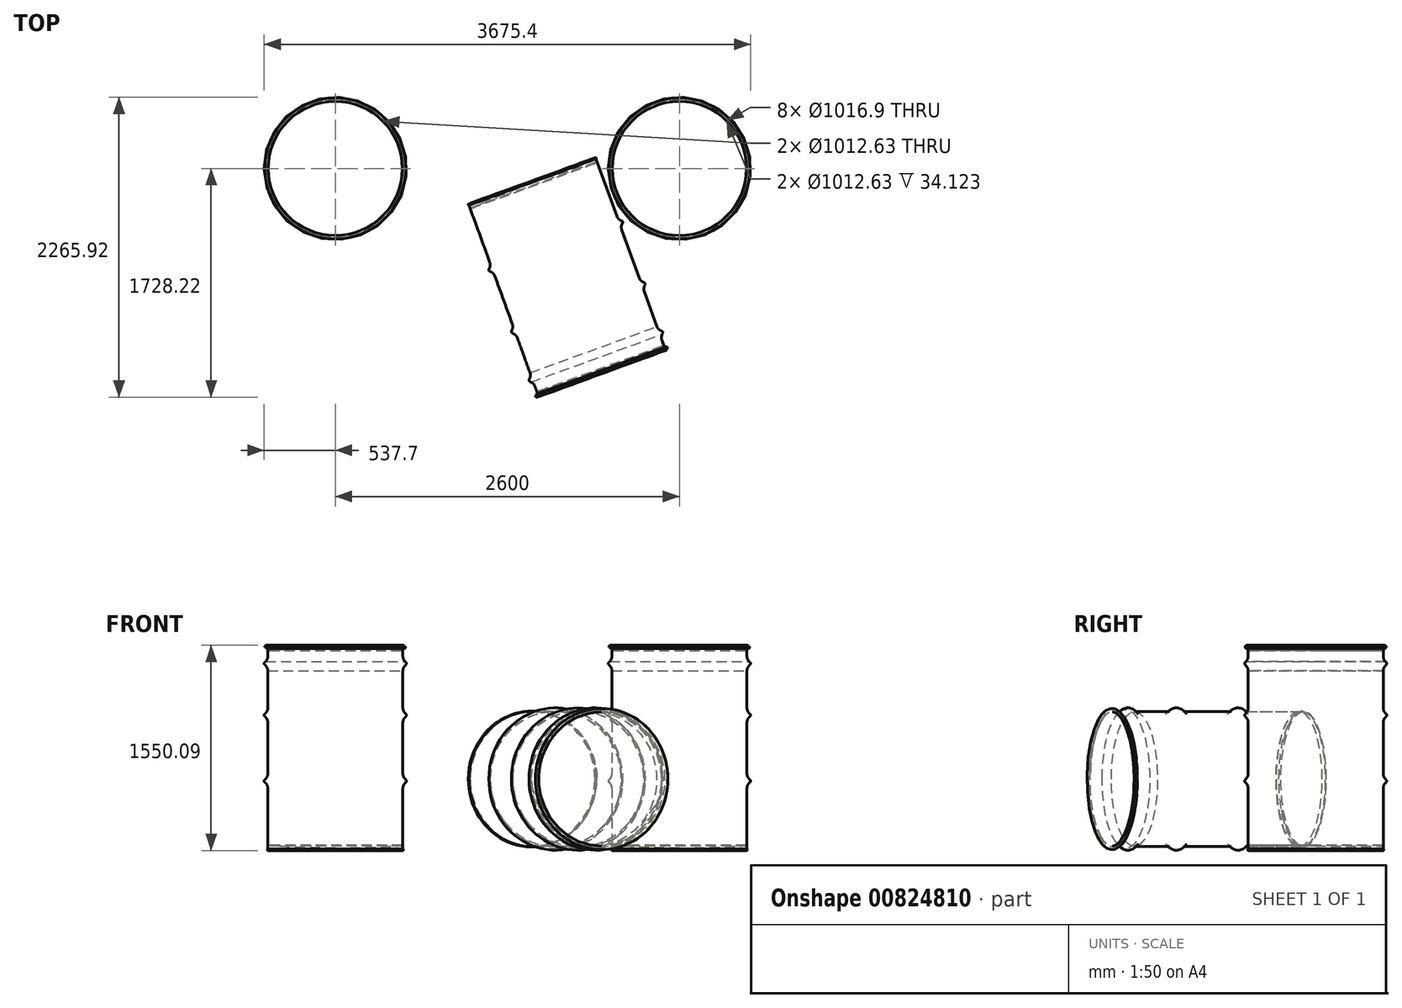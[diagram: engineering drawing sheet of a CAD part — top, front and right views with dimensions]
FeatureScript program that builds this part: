
annotation { "Feature Type Name" : "Feature", "Feature Type Description" : "" }
export const myFeature = defineFeature(function(context is Context, id is Id, definition is map)
    precondition{}
    {
        {
            var Q0;
            Q0=qCreatedBy(makeId("Front.planeOp"),FACE);
            var sketch = newSketch(context, id + "F0", { "sketchPlane" : qUnion([Q0])});
            skLineSegment(sketch, "E0.top", {"start": v(-286.95, 863.6) * mm, "end": v(-285.75, 863.6) * mm, "construction": true});
            skLineSegment(sketch, "E0.right", {"start": v(-285.75, 0) * mm, "end": v(-285.75, 264.7) * mm});
            skLineSegment(sketch, "E1", {"start": v(0, 0) * mm, "end": v(0, 177.34) * mm, "construction": true});
            skArc(sketch, "E2", {"start": v(-285.75, 863.6) * mm, "mid": v(-297.8, 866.42) * mm, "end": v(-288.25, 858.55) * mm});
            skArc(sketch, "E3", {"start": v(-286.95, 863.6) * mm, "mid": v(-296.72, 865.89) * mm, "end": v(-288.98, 859.5) * mm});
            skLineSegment(sketch, "E4", {"start": v(-288.98, 859.5) * mm, "end": v(-288.25, 858.55) * mm});
            skArc(sketch, "E5", {"start": v(-285.75, 0) * mm, "mid": v(-288.87, 2.56) * mm, "end": v(-286.95, 6.11) * mm});
            skLineSegment(sketch, "E6.trimOffspring", {"start": v(-286.95, 6.11) * mm, "end": v(-286.95, 264.7) * mm});
            skPoint(sketch, "E0.left.start.orphan", {"position": v(-286.95, 0) * mm});
            skLineSegment(sketch, "E7", {"start": v(-295.84, 802.73) * mm, "end": v(-300.33, 798.24) * mm});
            skLineSegment(sketch, "E8", {"start": v(-300.33, 789.26) * mm, "end": v(-295.84, 784.77) * mm});
            skLineSegment(sketch, "E9.trimOffspring", {"start": v(-286.95, 824.2) * mm, "end": v(-286.95, 863.6) * mm});
            skArc(sketch, "E10.filletArc", {"start": v(-300.33, 798.24) * mm, "mid": v(-302.2, 793.75) * mm, "end": v(-300.33, 789.26) * mm});
            skArc(sketch, "E11.filletArc", {"start": v(-295.84, 802.73) * mm, "mid": v(-289.26, 812.58) * mm, "end": v(-286.95, 824.2) * mm});
            skArc(sketch, "E12.filletArc", {"start": v(-286.95, 763.3) * mm, "mid": v(-289.26, 774.92) * mm, "end": v(-295.84, 784.77) * mm});
            skLineSegment(sketch, "E13", {"start": v(-302.19, 748.51) * mm, "end": v(-302.19, 170.1) * mm, "construction": true});
            skLineSegment(sketch, "E14", {"start": v(-292.1, 863.6) * mm, "end": v(-292.1, 869.95) * mm, "construction": true});
            skLineSegment(sketch, "E15", {"start": v(-300.33, 798.24) * mm, "end": v(-300.33, 789.26) * mm, "construction": true});
            skLineSegment(sketch, "E16", {"start": v(-295.84, 802.73) * mm, "end": v(-295.84, 784.77) * mm, "construction": true});
            skLineSegment(sketch, "E17", {"start": v(-286.95, 763.3) * mm, "end": v(-285.75, 763.3) * mm, "construction": true});
            skLineSegment(sketch, "E18", {"start": v(-286.95, 824.2) * mm, "end": v(-285.75, 824.2) * mm, "construction": true});
            skLineSegment(sketch, "E19.trimOffspring", {"start": v(-285.75, 824.2) * mm, "end": v(-285.75, 863.6) * mm});
            skLineSegment(sketch, "E20", {"start": v(-299.35, 790.24) * mm, "end": v(-294.86, 785.75) * mm});
            skLineSegment(sketch, "E21", {"start": v(-299.35, 797.26) * mm, "end": v(-294.86, 801.75) * mm});
            skArc(sketch, "E22", {"start": v(-299.35, 797.26) * mm, "mid": v(-300.8, 793.75) * mm, "end": v(-299.35, 790.24) * mm});
            skArc(sketch, "E23", {"start": v(-294.86, 801.75) * mm, "mid": v(-288.12, 812.08) * mm, "end": v(-285.75, 824.2) * mm});
            skArc(sketch, "E24", {"start": v(-285.75, 763.3) * mm, "mid": v(-288.03, 775.45) * mm, "end": v(-294.86, 785.75) * mm});
            skLineSegment(sketch, "E25", {"start": v(-295.84, 583.53) * mm, "end": v(-300.33, 579.04) * mm});
            skLineSegment(sketch, "E26", {"start": v(-300.33, 570.06) * mm, "end": v(-295.84, 565.57) * mm});
            skLineSegment(sketch, "E27.trimOffspring", {"start": v(-286.95, 605) * mm, "end": v(-286.95, 763.3) * mm});
            skPoint(sketch, "E28.visualSharp", {"position": v(-304.82, 574.55) * mm});
            skArc(sketch, "E28.filletArc", {"start": v(-300.33, 579.04) * mm, "mid": v(-302.2, 574.55) * mm, "end": v(-300.33, 570.06) * mm});
            skArc(sketch, "E29.filletArc", {"start": v(-295.84, 583.53) * mm, "mid": v(-289.26, 593.38) * mm, "end": v(-286.95, 605) * mm});
            skArc(sketch, "E30.filletArc", {"start": v(-286.95, 544.1) * mm, "mid": v(-289.26, 555.72) * mm, "end": v(-295.84, 565.57) * mm});
            skLineSegment(sketch, "E31", {"start": v(-295.84, 583.53) * mm, "end": v(-295.84, 565.57) * mm, "construction": true});
            skLineSegment(sketch, "E32", {"start": v(-286.95, 544.1) * mm, "end": v(-285.75, 544.1) * mm, "construction": true});
            skLineSegment(sketch, "E33", {"start": v(-286.95, 605) * mm, "end": v(-285.75, 605) * mm, "construction": true});
            skLineSegment(sketch, "E34.trimOffspring", {"start": v(-285.75, 605) * mm, "end": v(-285.75, 763.3) * mm});
            skLineSegment(sketch, "E35", {"start": v(-299.48, 578.19) * mm, "end": v(-295, 582.68) * mm});
            skArc(sketch, "E36", {"start": v(-295, 582.68) * mm, "mid": v(-288.15, 592.92) * mm, "end": v(-285.75, 605) * mm});
            skLineSegment(sketch, "E37", {"start": v(-299.48, 570.9) * mm, "end": v(-295, 566.42) * mm});
            skArc(sketch, "E38", {"start": v(-285.75, 544.1) * mm, "mid": v(-288.15, 556.18) * mm, "end": v(-295, 566.42) * mm});
            skArc(sketch, "E39", {"start": v(-299.48, 578.19) * mm, "mid": v(-301, 574.55) * mm, "end": v(-299.48, 570.9) * mm});
            skLineSegment(sketch, "E40", {"start": v(-295.84, 304.13) * mm, "end": v(-300.33, 299.64) * mm});
            skLineSegment(sketch, "E41", {"start": v(-300.33, 290.66) * mm, "end": v(-295.84, 286.17) * mm});
            skArc(sketch, "E42.filletArc", {"start": v(-300.33, 299.64) * mm, "mid": v(-302.19, 295.15) * mm, "end": v(-300.33, 290.66) * mm});
            skLineSegment(sketch, "E43.trimOffspring", {"start": v(-286.95, 325.6) * mm, "end": v(-286.95, 544.1) * mm});
            skArc(sketch, "E44.filletArc", {"start": v(-295.84, 304.13) * mm, "mid": v(-289.26, 313.98) * mm, "end": v(-286.95, 325.6) * mm});
            skArc(sketch, "E45.filletArc", {"start": v(-286.95, 264.7) * mm, "mid": v(-289.26, 276.32) * mm, "end": v(-295.84, 286.17) * mm});
            skLineSegment(sketch, "E46", {"start": v(-300.33, 299.64) * mm, "end": v(-300.33, 290.66) * mm, "construction": true});
            skLineSegment(sketch, "E47", {"start": v(-295.84, 304.13) * mm, "end": v(-295.84, 286.17) * mm, "construction": true});
            skLineSegment(sketch, "E48", {"start": v(-286.95, 325.6) * mm, "end": v(-285.75, 325.6) * mm, "construction": true});
            skLineSegment(sketch, "E49", {"start": v(-286.95, 264.7) * mm, "end": v(-285.75, 264.7) * mm, "construction": true});
            skLineSegment(sketch, "E50.trimOffspring", {"start": v(-285.75, 325.6) * mm, "end": v(-285.75, 544.1) * mm});
            skLineSegment(sketch, "E51", {"start": v(-299.48, 298.79) * mm, "end": v(-295, 303.28) * mm});
            skLineSegment(sketch, "E52", {"start": v(-299.48, 291.5) * mm, "end": v(-295, 287.02) * mm});
            skArc(sketch, "E53", {"start": v(-295, 303.28) * mm, "mid": v(-288.15, 313.52) * mm, "end": v(-285.75, 325.6) * mm});
            skArc(sketch, "E54", {"start": v(-285.75, 264.7) * mm, "mid": v(-288.15, 276.78) * mm, "end": v(-295, 287.02) * mm});
            skArc(sketch, "E55", {"start": v(-299.48, 298.79) * mm, "mid": v(-300.99, 295.15) * mm, "end": v(-299.48, 291.5) * mm});
            skLineSegment(sketch, "E56", {"start": v(0, 0) * mm, "end": v(-491.48, 0) * mm, "construction": true});
            skSolve(sketch);
        }
        {
            var Q0;
            Q0=qSketchRegion(id+"F0",true);
            var Q1;
            Q1=qConstructionFilter(qBodyType(qCreatedBy(id+"F0",EDGE),BodyType.WIRE),ConstructionObject.NO);
            var Q2;
            Q2=sQuery(id+"F0.wireOp",EDGE,"E1");
            revolve(context, id + "F1", {"entities" : qUnion([Q0]), "surfaceEntities" : qUnion([Q1]), "axis" : qUnion([Q2]), "revolveType" : RevolveType.FULL});
        }
        {
            var Q0;
            Q0=qCreatedBy(makeId("Front.planeOp"),FACE);
            var sketch = newSketch(context, id + "F2", { "sketchPlane" : qUnion([Q0])});
            skLineSegment(sketch, "E57", {"start": v(286.95, 6.11) * mm, "end": v(286.95, 264.7) * mm});
            skArc(sketch, "E58", {"start": v(285.75, 0) * mm, "mid": v(288.87, 2.56) * mm, "end": v(286.95, 6.11) * mm});
            skLineSegment(sketch, "E59", {"start": v(285.75, 0) * mm, "end": v(285.75, 264.7) * mm});
            skLineSegment(sketch, "E60", {"start": v(-285.75, 264.7) * mm, "end": v(-285.75, 0) * mm});
            skLineSegment(sketch, "E61", {"start": v(-285.75, 0) * mm, "end": v(-284.55, 0) * mm});
            skLineSegment(sketch, "E62", {"start": v(-284.55, 0) * mm, "end": v(-284.55, 19.18) * mm});
            skArc(sketch, "E63", {"start": v(-282.4, 21.14) * mm, "mid": v(-283.91, 20.63) * mm, "end": v(-284.55, 19.18) * mm});
            skLineSegment(sketch, "E64", {"start": v(0, 244.83) * mm, "end": v(0, -50.53) * mm, "construction": true});
            skArc(sketch, "E65", {"start": v(-282.4, 21.14) * mm, "mid": v(-141.33, 12.15) * mm, "end": v(0, 9.14) * mm});
            skLineSegment(sketch, "E66", {"start": v(0, 9.14) * mm, "end": v(0, 10.34) * mm});
            skArc(sketch, "E67", {"start": v(-285.75, 19.18) * mm, "mid": v(-284.72, 21.52) * mm, "end": v(-282.3, 22.34) * mm});
            skArc(sketch, "E68", {"start": v(-282.3, 22.34) * mm, "mid": v(-141.28, 13.34) * mm, "end": v(0, 10.34) * mm});
            skLineSegment(sketch, "E69", {"start": v(-282.58, 19.18) * mm, "end": v(-282.58, 22.35) * mm, "construction": true});
            skSolve(sketch);
        }
        {
            var Q0;
            Q0=qSketchRegion(id+"F2",true);
            var Q1;
            Q1=sQuery(id+"F2.wireOp",EDGE,"E64");
            revolve(context, id + "F3", {"operationType" : NewBodyOperationType.ADD, "entities" : qUnion([Q0]), "axis" : qUnion([Q1]), "revolveType" : RevolveType.FULL});
        }
        {
            var Q0;
            Q0=qCreatedBy(makeId("Front.planeOp"),FACE);
            var sketch = newSketch(context, id + "F4", { "sketchPlane" : qUnion([Q0])});
            skLineSegment(sketch, "E70", {"start": v(0, 998.16) * mm, "end": v(0, -198.69) * mm, "construction": true});
            skArc(sketch, "E71", {"start": v(-288.25, 858.55) * mm, "mid": v(-297.8, 866.42) * mm, "end": v(-285.75, 863.6) * mm, "construction": true});
            skLineSegment(sketch, "E72", {"start": v(-285.75, 863.6) * mm, "end": v(-285.75, 824.2) * mm, "construction": true});
            skArc(sketch, "E73", {"start": v(-298.45, 863.6) * mm, "mid": v(-292.1, 869.95) * mm, "end": v(-285.75, 863.6) * mm});
            skLineSegment(sketch, "E74", {"start": v(-285.75, 863.6) * mm, "end": v(-285.75, 855.15) * mm});
            skArc(sketch, "E75", {"start": v(-285.75, 855.15) * mm, "mid": v(-283.75, 850.52) * mm, "end": v(-279.02, 848.8) * mm});
            skArc(sketch, "E76", {"start": v(-279.02, 848.8) * mm, "mid": v(-139.57, 855.14) * mm, "end": v(0, 857.25) * mm});
            skLineSegment(sketch, "E77", {"start": v(-298.45, 863.6) * mm, "end": v(-299.65, 863.6) * mm});
            skArc(sketch, "E78", {"start": v(-299.65, 863.6) * mm, "mid": v(-292.1, 871.15) * mm, "end": v(-284.55, 863.6) * mm});
            skLineSegment(sketch, "E79", {"start": v(-284.55, 863.6) * mm, "end": v(-284.55, 855.15) * mm});
            skArc(sketch, "E80", {"start": v(-284.55, 855.15) * mm, "mid": v(-282.93, 851.4) * mm, "end": v(-279.09, 850) * mm});
            skArc(sketch, "E81", {"start": v(-279.09, 850) * mm, "mid": v(-139.6, 856.34) * mm, "end": v(0, 858.45) * mm});
            skLineSegment(sketch, "E82", {"start": v(0, 858.45) * mm, "end": v(0, 857.25) * mm});
            skLineSegment(sketch, "E83", {"start": v(-279.4, 855.15) * mm, "end": v(-279.02, 848.8) * mm, "construction": true});
            skLineSegment(sketch, "E84", {"start": v(-279.4, 855.15) * mm, "end": v(-279.4, 848.8) * mm, "construction": true});
            skLineSegment(sketch, "E85", {"start": v(-292.1, 863.6) * mm, "end": v(-292.1, 871.15) * mm, "construction": true});
            skSolve(sketch);
        }
        {
            var Q0;
            Q0=qSketchRegion(id+"F4",true);
            var Q1;
            Q1=sQuery(id+"F4.wireOp",EDGE,"E70");
            revolve(context, id + "F5", {"entities" : qUnion([Q0]), "axis" : qUnion([Q1]), "revolveType" : RevolveType.FULL});
        }
        {
            var Q0;
            Q0=makeQuery(id+"F5.opRevolve","SWEPT_BODY",BODY,{"disambiguationData":[OSD([sQuery(id+"F4.wireOp",EDGE,"E73"),sQuery(id+"F4.wireOp",EDGE,"E74"),sQuery(id+"F4.wireOp",EDGE,"E75"),sQuery(id+"F4.wireOp",EDGE,"E76"),sQuery(id+"F4.wireOp",EDGE,"E77"),sQuery(id+"F4.wireOp",EDGE,"E78"),sQuery(id+"F4.wireOp",EDGE,"E79"),sQuery(id+"F4.wireOp",EDGE,"E80"),sQuery(id+"F4.wireOp",EDGE,"E81"),sQuery(id+"F4.wireOp",EDGE,"E82")])]});
            var Q1;
            Q1=makeQuery(id+"F1.opRevolve","SWEPT_BODY",BODY,{"disambiguationData":[OSD([sQuery(id+"F0.wireOp",EDGE,"E0.right"),sQuery(id+"F0.wireOp",EDGE,"E2"),sQuery(id+"F0.wireOp",EDGE,"E3"),sQuery(id+"F0.wireOp",EDGE,"E4"),sQuery(id+"F0.wireOp",EDGE,"E5"),sQuery(id+"F0.wireOp",EDGE,"E6.trimOffspring"),sQuery(id+"F0.wireOp",EDGE,"E7"),sQuery(id+"F0.wireOp",EDGE,"E8"),sQuery(id+"F0.wireOp",EDGE,"E9.trimOffspring"),sQuery(id+"F0.wireOp",EDGE,"E10.filletArc"),sQuery(id+"F0.wireOp",EDGE,"E11.filletArc"),sQuery(id+"F0.wireOp",EDGE,"E12.filletArc"),sQuery(id+"F0.wireOp",EDGE,"E19.trimOffspring"),sQuery(id+"F0.wireOp",EDGE,"E20"),sQuery(id+"F0.wireOp",EDGE,"E21"),sQuery(id+"F0.wireOp",EDGE,"E22"),sQuery(id+"F0.wireOp",EDGE,"E23"),sQuery(id+"F0.wireOp",EDGE,"E24"),sQuery(id+"F0.wireOp",EDGE,"E25"),sQuery(id+"F0.wireOp",EDGE,"E26"),sQuery(id+"F0.wireOp",EDGE,"E27.trimOffspring"),sQuery(id+"F0.wireOp",EDGE,"E28.filletArc"),sQuery(id+"F0.wireOp",EDGE,"E29.filletArc"),sQuery(id+"F0.wireOp",EDGE,"E30.filletArc"),sQuery(id+"F0.wireOp",EDGE,"E34.trimOffspring"),sQuery(id+"F0.wireOp",EDGE,"E35"),sQuery(id+"F0.wireOp",EDGE,"E36"),sQuery(id+"F0.wireOp",EDGE,"E37"),sQuery(id+"F0.wireOp",EDGE,"E38"),sQuery(id+"F0.wireOp",EDGE,"E39"),sQuery(id+"F0.wireOp",EDGE,"E40"),sQuery(id+"F0.wireOp",EDGE,"E41"),sQuery(id+"F0.wireOp",EDGE,"E42.filletArc"),sQuery(id+"F0.wireOp",EDGE,"E43.trimOffspring"),sQuery(id+"F0.wireOp",EDGE,"E44.filletArc"),sQuery(id+"F0.wireOp",EDGE,"E45.filletArc"),sQuery(id+"F0.wireOp",EDGE,"E50.trimOffspring"),sQuery(id+"F0.wireOp",EDGE,"E51"),sQuery(id+"F0.wireOp",EDGE,"E52"),sQuery(id+"F0.wireOp",EDGE,"E53"),sQuery(id+"F0.wireOp",EDGE,"E54"),sQuery(id+"F0.wireOp",EDGE,"E55")])]});
            var Q2;
            Q2=qCreatedBy(makeId("Origin.pointOp"),VERTEX);
            transform(context, id + "F6", {"entities" : qUnion([Q0, Q1]), "transformType" : TransformType.SCALE_UNIFORMLY, "scale" : 1.78, "scalePoint" : qUnion([Q2]), "makeCopy" : false});
        }
        {
            var Q0;
            Q0=makeQuery(id+"F1.opRevolve","SWEPT_BODY",BODY,{"disambiguationData":[OSD([sQuery(id+"F0.wireOp",EDGE,"E0.right"),sQuery(id+"F0.wireOp",EDGE,"E2"),sQuery(id+"F0.wireOp",EDGE,"E3"),sQuery(id+"F0.wireOp",EDGE,"E4"),sQuery(id+"F0.wireOp",EDGE,"E5"),sQuery(id+"F0.wireOp",EDGE,"E6.trimOffspring"),sQuery(id+"F0.wireOp",EDGE,"E7"),sQuery(id+"F0.wireOp",EDGE,"E8"),sQuery(id+"F0.wireOp",EDGE,"E9.trimOffspring"),sQuery(id+"F0.wireOp",EDGE,"E10.filletArc"),sQuery(id+"F0.wireOp",EDGE,"E11.filletArc"),sQuery(id+"F0.wireOp",EDGE,"E12.filletArc"),sQuery(id+"F0.wireOp",EDGE,"E19.trimOffspring"),sQuery(id+"F0.wireOp",EDGE,"E20"),sQuery(id+"F0.wireOp",EDGE,"E21"),sQuery(id+"F0.wireOp",EDGE,"E22"),sQuery(id+"F0.wireOp",EDGE,"E23"),sQuery(id+"F0.wireOp",EDGE,"E24"),sQuery(id+"F0.wireOp",EDGE,"E25"),sQuery(id+"F0.wireOp",EDGE,"E26"),sQuery(id+"F0.wireOp",EDGE,"E27.trimOffspring"),sQuery(id+"F0.wireOp",EDGE,"E28.filletArc"),sQuery(id+"F0.wireOp",EDGE,"E29.filletArc"),sQuery(id+"F0.wireOp",EDGE,"E30.filletArc"),sQuery(id+"F0.wireOp",EDGE,"E34.trimOffspring"),sQuery(id+"F0.wireOp",EDGE,"E35"),sQuery(id+"F0.wireOp",EDGE,"E36"),sQuery(id+"F0.wireOp",EDGE,"E37"),sQuery(id+"F0.wireOp",EDGE,"E38"),sQuery(id+"F0.wireOp",EDGE,"E39"),sQuery(id+"F0.wireOp",EDGE,"E40"),sQuery(id+"F0.wireOp",EDGE,"E41"),sQuery(id+"F0.wireOp",EDGE,"E42.filletArc"),sQuery(id+"F0.wireOp",EDGE,"E43.trimOffspring"),sQuery(id+"F0.wireOp",EDGE,"E44.filletArc"),sQuery(id+"F0.wireOp",EDGE,"E45.filletArc"),sQuery(id+"F0.wireOp",EDGE,"E50.trimOffspring"),sQuery(id+"F0.wireOp",EDGE,"E51"),sQuery(id+"F0.wireOp",EDGE,"E52"),sQuery(id+"F0.wireOp",EDGE,"E53"),sQuery(id+"F0.wireOp",EDGE,"E54"),sQuery(id+"F0.wireOp",EDGE,"E55")])]});
            var Q1;
            Q1=makeQuery(id+"F5.opRevolve","SWEPT_BODY",BODY,{"disambiguationData":[OSD([sQuery(id+"F4.wireOp",EDGE,"E73"),sQuery(id+"F4.wireOp",EDGE,"E74"),sQuery(id+"F4.wireOp",EDGE,"E75"),sQuery(id+"F4.wireOp",EDGE,"E76"),sQuery(id+"F4.wireOp",EDGE,"E77"),sQuery(id+"F4.wireOp",EDGE,"E78"),sQuery(id+"F4.wireOp",EDGE,"E79"),sQuery(id+"F4.wireOp",EDGE,"E80"),sQuery(id+"F4.wireOp",EDGE,"E81"),sQuery(id+"F4.wireOp",EDGE,"E82")])]});
            transform(context, id + "F7", {"entities" : qUnion([Q0, Q1]), "transformType" : TransformType.TRANSLATION_3D, "dx" : 2600 * mm, "dy" : 0 * mm, "dz" : 0 * mm, "makeCopy" : true});
        }
        {
            var Q0;
            Q0=makeQuery(id+"F7.opPattern","COPY",BODY,{"derivedFrom":makeQuery(id+"F5.opRevolve","SWEPT_BODY",BODY,{"disambiguationData":[OSD([sQuery(id+"F4.wireOp",EDGE,"E73"),sQuery(id+"F4.wireOp",EDGE,"E74"),sQuery(id+"F4.wireOp",EDGE,"E75"),sQuery(id+"F4.wireOp",EDGE,"E76"),sQuery(id+"F4.wireOp",EDGE,"E77"),sQuery(id+"F4.wireOp",EDGE,"E78"),sQuery(id+"F4.wireOp",EDGE,"E79"),sQuery(id+"F4.wireOp",EDGE,"E80"),sQuery(id+"F4.wireOp",EDGE,"E81"),sQuery(id+"F4.wireOp",EDGE,"E82")])]}),"instanceName":"1"});
            var Q1;
            Q1=makeQuery(id+"F7.opPattern","COPY",BODY,{"derivedFrom":makeQuery(id+"F1.opRevolve","SWEPT_BODY",BODY,{"disambiguationData":[OSD([sQuery(id+"F0.wireOp",EDGE,"E0.right"),sQuery(id+"F0.wireOp",EDGE,"E2"),sQuery(id+"F0.wireOp",EDGE,"E3"),sQuery(id+"F0.wireOp",EDGE,"E4"),sQuery(id+"F0.wireOp",EDGE,"E5"),sQuery(id+"F0.wireOp",EDGE,"E6.trimOffspring"),sQuery(id+"F0.wireOp",EDGE,"E7"),sQuery(id+"F0.wireOp",EDGE,"E8"),sQuery(id+"F0.wireOp",EDGE,"E9.trimOffspring"),sQuery(id+"F0.wireOp",EDGE,"E10.filletArc"),sQuery(id+"F0.wireOp",EDGE,"E11.filletArc"),sQuery(id+"F0.wireOp",EDGE,"E12.filletArc"),sQuery(id+"F0.wireOp",EDGE,"E19.trimOffspring"),sQuery(id+"F0.wireOp",EDGE,"E20"),sQuery(id+"F0.wireOp",EDGE,"E21"),sQuery(id+"F0.wireOp",EDGE,"E22"),sQuery(id+"F0.wireOp",EDGE,"E23"),sQuery(id+"F0.wireOp",EDGE,"E24"),sQuery(id+"F0.wireOp",EDGE,"E25"),sQuery(id+"F0.wireOp",EDGE,"E26"),sQuery(id+"F0.wireOp",EDGE,"E27.trimOffspring"),sQuery(id+"F0.wireOp",EDGE,"E28.filletArc"),sQuery(id+"F0.wireOp",EDGE,"E29.filletArc"),sQuery(id+"F0.wireOp",EDGE,"E30.filletArc"),sQuery(id+"F0.wireOp",EDGE,"E34.trimOffspring"),sQuery(id+"F0.wireOp",EDGE,"E35"),sQuery(id+"F0.wireOp",EDGE,"E36"),sQuery(id+"F0.wireOp",EDGE,"E37"),sQuery(id+"F0.wireOp",EDGE,"E38"),sQuery(id+"F0.wireOp",EDGE,"E39"),sQuery(id+"F0.wireOp",EDGE,"E40"),sQuery(id+"F0.wireOp",EDGE,"E41"),sQuery(id+"F0.wireOp",EDGE,"E42.filletArc"),sQuery(id+"F0.wireOp",EDGE,"E43.trimOffspring"),sQuery(id+"F0.wireOp",EDGE,"E44.filletArc"),sQuery(id+"F0.wireOp",EDGE,"E45.filletArc"),sQuery(id+"F0.wireOp",EDGE,"E50.trimOffspring"),sQuery(id+"F0.wireOp",EDGE,"E51"),sQuery(id+"F0.wireOp",EDGE,"E52"),sQuery(id+"F0.wireOp",EDGE,"E53"),sQuery(id+"F0.wireOp",EDGE,"E54"),sQuery(id+"F0.wireOp",EDGE,"E55")])]}),"instanceName":"1"});
            transform(context, id + "F8", {"entities" : qUnion([Q0, Q1]), "transformType" : TransformType.TRANSLATION_3D, "dx" : -1000 * mm, "dy" : -500 * mm, "dz" : 0 * mm, "makeCopy" : true});
        }
        {
            var Q0;
            Q0=makeQuery(id+"F8.opPattern","COPY",BODY,{"derivedFrom":makeQuery(id+"F7.opPattern","COPY",BODY,{"derivedFrom":makeQuery(id+"F5.opRevolve","SWEPT_BODY",BODY,{"disambiguationData":[OSD([sQuery(id+"F4.wireOp",EDGE,"E73"),sQuery(id+"F4.wireOp",EDGE,"E74"),sQuery(id+"F4.wireOp",EDGE,"E75"),sQuery(id+"F4.wireOp",EDGE,"E76"),sQuery(id+"F4.wireOp",EDGE,"E77"),sQuery(id+"F4.wireOp",EDGE,"E78"),sQuery(id+"F4.wireOp",EDGE,"E79"),sQuery(id+"F4.wireOp",EDGE,"E80"),sQuery(id+"F4.wireOp",EDGE,"E81"),sQuery(id+"F4.wireOp",EDGE,"E82")])]}),"instanceName":"1"}),"instanceName":"1"});
            var Q1;
            Q1=makeQuery(id+"F8.opPattern","COPY",BODY,{"derivedFrom":makeQuery(id+"F7.opPattern","COPY",BODY,{"derivedFrom":makeQuery(id+"F1.opRevolve","SWEPT_BODY",BODY,{"disambiguationData":[OSD([sQuery(id+"F0.wireOp",EDGE,"E0.right"),sQuery(id+"F0.wireOp",EDGE,"E2"),sQuery(id+"F0.wireOp",EDGE,"E3"),sQuery(id+"F0.wireOp",EDGE,"E4"),sQuery(id+"F0.wireOp",EDGE,"E5"),sQuery(id+"F0.wireOp",EDGE,"E6.trimOffspring"),sQuery(id+"F0.wireOp",EDGE,"E7"),sQuery(id+"F0.wireOp",EDGE,"E8"),sQuery(id+"F0.wireOp",EDGE,"E9.trimOffspring"),sQuery(id+"F0.wireOp",EDGE,"E10.filletArc"),sQuery(id+"F0.wireOp",EDGE,"E11.filletArc"),sQuery(id+"F0.wireOp",EDGE,"E12.filletArc"),sQuery(id+"F0.wireOp",EDGE,"E19.trimOffspring"),sQuery(id+"F0.wireOp",EDGE,"E20"),sQuery(id+"F0.wireOp",EDGE,"E21"),sQuery(id+"F0.wireOp",EDGE,"E22"),sQuery(id+"F0.wireOp",EDGE,"E23"),sQuery(id+"F0.wireOp",EDGE,"E24"),sQuery(id+"F0.wireOp",EDGE,"E25"),sQuery(id+"F0.wireOp",EDGE,"E26"),sQuery(id+"F0.wireOp",EDGE,"E27.trimOffspring"),sQuery(id+"F0.wireOp",EDGE,"E28.filletArc"),sQuery(id+"F0.wireOp",EDGE,"E29.filletArc"),sQuery(id+"F0.wireOp",EDGE,"E30.filletArc"),sQuery(id+"F0.wireOp",EDGE,"E34.trimOffspring"),sQuery(id+"F0.wireOp",EDGE,"E35"),sQuery(id+"F0.wireOp",EDGE,"E36"),sQuery(id+"F0.wireOp",EDGE,"E37"),sQuery(id+"F0.wireOp",EDGE,"E38"),sQuery(id+"F0.wireOp",EDGE,"E39"),sQuery(id+"F0.wireOp",EDGE,"E40"),sQuery(id+"F0.wireOp",EDGE,"E41"),sQuery(id+"F0.wireOp",EDGE,"E42.filletArc"),sQuery(id+"F0.wireOp",EDGE,"E43.trimOffspring"),sQuery(id+"F0.wireOp",EDGE,"E44.filletArc"),sQuery(id+"F0.wireOp",EDGE,"E45.filletArc"),sQuery(id+"F0.wireOp",EDGE,"E50.trimOffspring"),sQuery(id+"F0.wireOp",EDGE,"E51"),sQuery(id+"F0.wireOp",EDGE,"E52"),sQuery(id+"F0.wireOp",EDGE,"E53"),sQuery(id+"F0.wireOp",EDGE,"E54"),sQuery(id+"F0.wireOp",EDGE,"E55")])]}),"instanceName":"1"}),"instanceName":"1"});
            var Q2;
            Q2=sQuery(id+"F0.wireOp",EDGE,"E56");
            transform(context, id + "F9", {"entities" : qUnion([Q0, Q1]), "transformType" : TransformType.ROTATION, "transformAxis" : qUnion([Q2]), "angle" : 90 * degree, "oppositeDirection" : true, "makeCopy" : false});
        }
        {
            var Q0;
            Q0=makeQuery(id+"F8.opPattern","COPY",BODY,{"derivedFrom":makeQuery(id+"F7.opPattern","COPY",BODY,{"derivedFrom":makeQuery(id+"F1.opRevolve","SWEPT_BODY",BODY,{"disambiguationData":[OSD([sQuery(id+"F0.wireOp",EDGE,"E0.right"),sQuery(id+"F0.wireOp",EDGE,"E2"),sQuery(id+"F0.wireOp",EDGE,"E3"),sQuery(id+"F0.wireOp",EDGE,"E4"),sQuery(id+"F0.wireOp",EDGE,"E5"),sQuery(id+"F0.wireOp",EDGE,"E6.trimOffspring"),sQuery(id+"F0.wireOp",EDGE,"E7"),sQuery(id+"F0.wireOp",EDGE,"E8"),sQuery(id+"F0.wireOp",EDGE,"E9.trimOffspring"),sQuery(id+"F0.wireOp",EDGE,"E10.filletArc"),sQuery(id+"F0.wireOp",EDGE,"E11.filletArc"),sQuery(id+"F0.wireOp",EDGE,"E12.filletArc"),sQuery(id+"F0.wireOp",EDGE,"E19.trimOffspring"),sQuery(id+"F0.wireOp",EDGE,"E20"),sQuery(id+"F0.wireOp",EDGE,"E21"),sQuery(id+"F0.wireOp",EDGE,"E22"),sQuery(id+"F0.wireOp",EDGE,"E23"),sQuery(id+"F0.wireOp",EDGE,"E24"),sQuery(id+"F0.wireOp",EDGE,"E25"),sQuery(id+"F0.wireOp",EDGE,"E26"),sQuery(id+"F0.wireOp",EDGE,"E27.trimOffspring"),sQuery(id+"F0.wireOp",EDGE,"E28.filletArc"),sQuery(id+"F0.wireOp",EDGE,"E29.filletArc"),sQuery(id+"F0.wireOp",EDGE,"E30.filletArc"),sQuery(id+"F0.wireOp",EDGE,"E34.trimOffspring"),sQuery(id+"F0.wireOp",EDGE,"E35"),sQuery(id+"F0.wireOp",EDGE,"E36"),sQuery(id+"F0.wireOp",EDGE,"E37"),sQuery(id+"F0.wireOp",EDGE,"E38"),sQuery(id+"F0.wireOp",EDGE,"E39"),sQuery(id+"F0.wireOp",EDGE,"E40"),sQuery(id+"F0.wireOp",EDGE,"E41"),sQuery(id+"F0.wireOp",EDGE,"E42.filletArc"),sQuery(id+"F0.wireOp",EDGE,"E43.trimOffspring"),sQuery(id+"F0.wireOp",EDGE,"E44.filletArc"),sQuery(id+"F0.wireOp",EDGE,"E45.filletArc"),sQuery(id+"F0.wireOp",EDGE,"E50.trimOffspring"),sQuery(id+"F0.wireOp",EDGE,"E51"),sQuery(id+"F0.wireOp",EDGE,"E52"),sQuery(id+"F0.wireOp",EDGE,"E53"),sQuery(id+"F0.wireOp",EDGE,"E54"),sQuery(id+"F0.wireOp",EDGE,"E55")])]}),"instanceName":"1"}),"instanceName":"1"});
            var Q1;
            Q1=makeQuery(id+"F8.opPattern","COPY",BODY,{"derivedFrom":makeQuery(id+"F7.opPattern","COPY",BODY,{"derivedFrom":makeQuery(id+"F5.opRevolve","SWEPT_BODY",BODY,{"disambiguationData":[OSD([sQuery(id+"F4.wireOp",EDGE,"E73"),sQuery(id+"F4.wireOp",EDGE,"E74"),sQuery(id+"F4.wireOp",EDGE,"E75"),sQuery(id+"F4.wireOp",EDGE,"E76"),sQuery(id+"F4.wireOp",EDGE,"E77"),sQuery(id+"F4.wireOp",EDGE,"E78"),sQuery(id+"F4.wireOp",EDGE,"E79"),sQuery(id+"F4.wireOp",EDGE,"E80"),sQuery(id+"F4.wireOp",EDGE,"E81"),sQuery(id+"F4.wireOp",EDGE,"E82")])]}),"instanceName":"1"}),"instanceName":"1"});
            var Q2;
            Q2=sQuery(id+"F0.wireOp",EDGE,"E50.trimOffspring");
            transform(context, id + "F10", {"entities" : qUnion([Q0, Q1]), "transformType" : TransformType.ROTATION, "transformAxis" : qUnion([Q2]), "angle" : 20 * degree, "makeCopy" : false});
        }
        {
            var Q0;
            Q0=makeQuery(id+"F8.opPattern","COPY",BODY,{"derivedFrom":makeQuery(id+"F7.opPattern","COPY",BODY,{"derivedFrom":makeQuery(id+"F5.opRevolve","SWEPT_BODY",BODY,{"disambiguationData":[OSD([sQuery(id+"F4.wireOp",EDGE,"E73"),sQuery(id+"F4.wireOp",EDGE,"E74"),sQuery(id+"F4.wireOp",EDGE,"E75"),sQuery(id+"F4.wireOp",EDGE,"E76"),sQuery(id+"F4.wireOp",EDGE,"E77"),sQuery(id+"F4.wireOp",EDGE,"E78"),sQuery(id+"F4.wireOp",EDGE,"E79"),sQuery(id+"F4.wireOp",EDGE,"E80"),sQuery(id+"F4.wireOp",EDGE,"E81"),sQuery(id+"F4.wireOp",EDGE,"E82")])]}),"instanceName":"1"}),"instanceName":"1"});
            var Q1;
            Q1=makeQuery(id+"F8.opPattern","COPY",BODY,{"derivedFrom":makeQuery(id+"F7.opPattern","COPY",BODY,{"derivedFrom":makeQuery(id+"F1.opRevolve","SWEPT_BODY",BODY,{"disambiguationData":[OSD([sQuery(id+"F0.wireOp",EDGE,"E0.right"),sQuery(id+"F0.wireOp",EDGE,"E2"),sQuery(id+"F0.wireOp",EDGE,"E3"),sQuery(id+"F0.wireOp",EDGE,"E4"),sQuery(id+"F0.wireOp",EDGE,"E5"),sQuery(id+"F0.wireOp",EDGE,"E6.trimOffspring"),sQuery(id+"F0.wireOp",EDGE,"E7"),sQuery(id+"F0.wireOp",EDGE,"E8"),sQuery(id+"F0.wireOp",EDGE,"E9.trimOffspring"),sQuery(id+"F0.wireOp",EDGE,"E10.filletArc"),sQuery(id+"F0.wireOp",EDGE,"E11.filletArc"),sQuery(id+"F0.wireOp",EDGE,"E12.filletArc"),sQuery(id+"F0.wireOp",EDGE,"E19.trimOffspring"),sQuery(id+"F0.wireOp",EDGE,"E20"),sQuery(id+"F0.wireOp",EDGE,"E21"),sQuery(id+"F0.wireOp",EDGE,"E22"),sQuery(id+"F0.wireOp",EDGE,"E23"),sQuery(id+"F0.wireOp",EDGE,"E24"),sQuery(id+"F0.wireOp",EDGE,"E25"),sQuery(id+"F0.wireOp",EDGE,"E26"),sQuery(id+"F0.wireOp",EDGE,"E27.trimOffspring"),sQuery(id+"F0.wireOp",EDGE,"E28.filletArc"),sQuery(id+"F0.wireOp",EDGE,"E29.filletArc"),sQuery(id+"F0.wireOp",EDGE,"E30.filletArc"),sQuery(id+"F0.wireOp",EDGE,"E34.trimOffspring"),sQuery(id+"F0.wireOp",EDGE,"E35"),sQuery(id+"F0.wireOp",EDGE,"E36"),sQuery(id+"F0.wireOp",EDGE,"E37"),sQuery(id+"F0.wireOp",EDGE,"E38"),sQuery(id+"F0.wireOp",EDGE,"E39"),sQuery(id+"F0.wireOp",EDGE,"E40"),sQuery(id+"F0.wireOp",EDGE,"E41"),sQuery(id+"F0.wireOp",EDGE,"E42.filletArc"),sQuery(id+"F0.wireOp",EDGE,"E43.trimOffspring"),sQuery(id+"F0.wireOp",EDGE,"E44.filletArc"),sQuery(id+"F0.wireOp",EDGE,"E45.filletArc"),sQuery(id+"F0.wireOp",EDGE,"E50.trimOffspring"),sQuery(id+"F0.wireOp",EDGE,"E51"),sQuery(id+"F0.wireOp",EDGE,"E52"),sQuery(id+"F0.wireOp",EDGE,"E53"),sQuery(id+"F0.wireOp",EDGE,"E54"),sQuery(id+"F0.wireOp",EDGE,"E55")])]}),"instanceName":"1"}),"instanceName":"1"});
            transform(context, id + "F11", {"entities" : qUnion([Q0, Q1]), "transformType" : TransformType.TRANSLATION_3D, "dx" : 0 * mm, "dy" : -738 * mm, "dz" : 1040 * mm, "makeCopy" : false});
        }
    });
